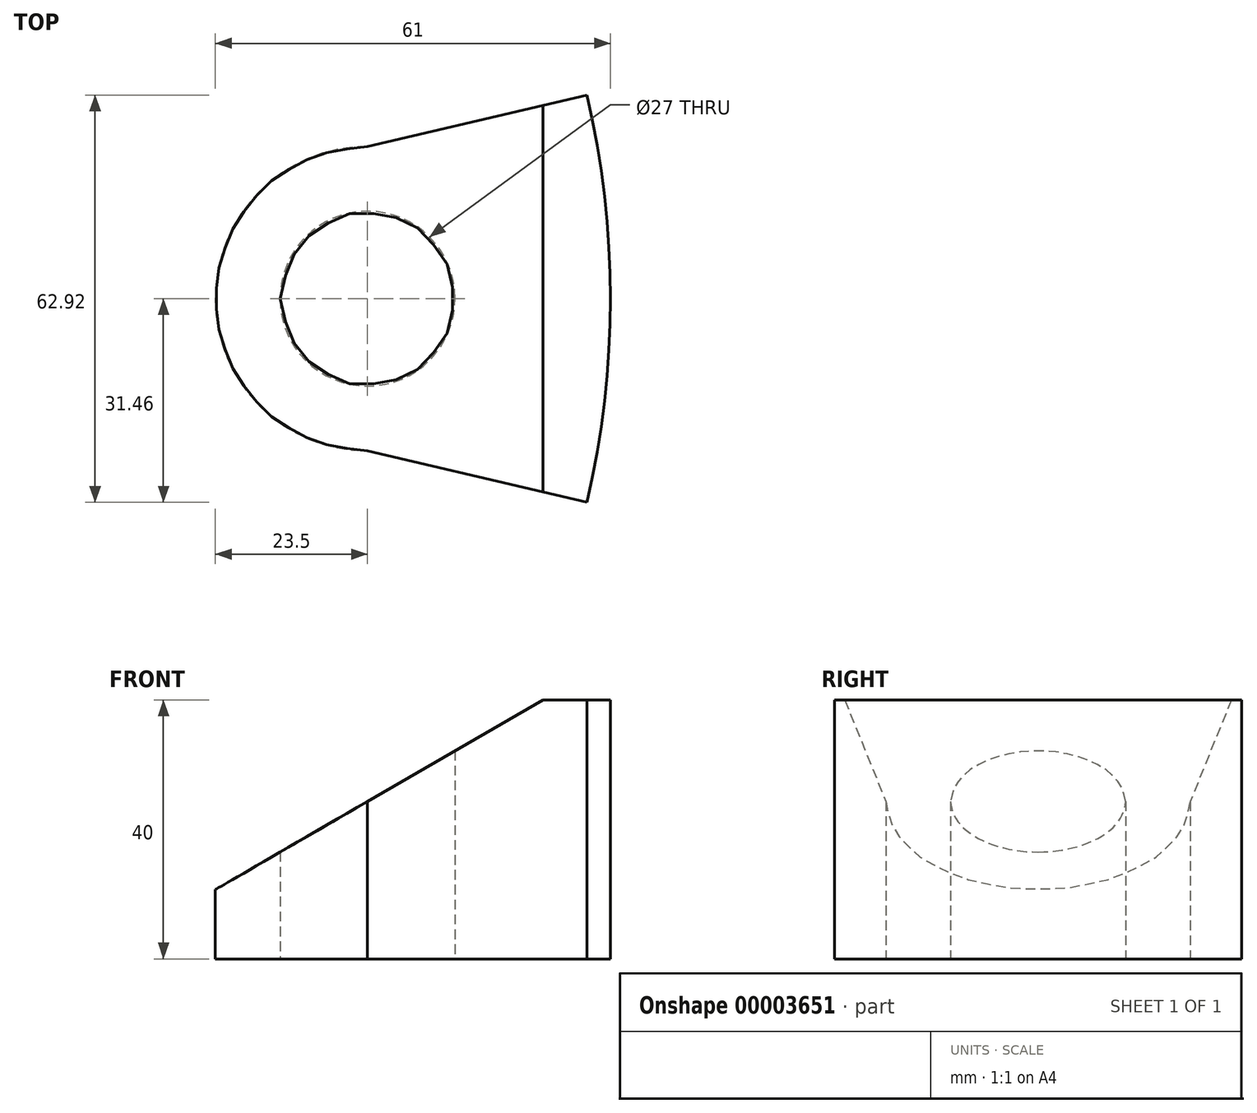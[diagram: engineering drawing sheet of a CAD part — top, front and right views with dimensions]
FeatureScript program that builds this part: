
annotation { "Feature Type Name" : "Feature", "Feature Type Description" : "" }
export const myFeature = defineFeature(function(context is Context, id is Id, definition is map)
    precondition{}
    {
        {
            var Q0;
            Q0=qCreatedBy(makeId("Top.planeOp"),FACE);
            var sketch = newSketch(context, id + "F0", { "sketchPlane" : qUnion([Q0])});
            skArc(sketch, "E0", {"start": v(133.85, -31.46) * mm, "mid": v(137.5, 0) * mm, "end": v(133.85, 31.46) * mm});
            skArc(sketch, "E1", {"start": v(128.99, -30.31) * mm, "mid": v(132.5, 0) * mm, "end": v(128.99, 30.31) * mm});
            skLineSegment(sketch, "E2", {"start": v(137.5, 0) * mm, "end": v(113.5, 0) * mm, "construction": true});
            skCircle(sketch, "E3", {"center": v(100, 0) * mm, "radius": 13.5 * mm});
            skArc(sketch, "E4.0", {"start": v(100, 23.5) * mm, "mid": v(76.5, 0) * mm, "end": v(100, -23.5) * mm});
            skLineSegment(sketch, "E5", {"start": v(100, 23.5) * mm, "end": v(128.99, 30.31) * mm});
            skLineSegment(sketch, "E6.0.MirrorCS", {"start": v(100, -23.5) * mm, "end": v(128.99, -30.31) * mm});
            skLineSegment(sketch, "E7", {"start": v(128.99, 30.31) * mm, "end": v(133.85, 31.46) * mm});
            skLineSegment(sketch, "E8.0.MirrorCS", {"start": v(128.99, -30.31) * mm, "end": v(133.85, -31.46) * mm});
            skSolve(sketch);
        }
        {
            var Q0;
            Q0 = qSketchRegion(id + "F0", true);
            extrude(context, id + "F1", {"entities" : qUnion([Q0]), "depth" : 40 * mm});
        }
        {
            var Q0;
            Q0=qCreatedBy(makeId("Front.planeOp"),FACE);
            cPlane(context, id + "F2", {"entities" : qUnion([Q0]), "cplaneType" : CPlaneType.OFFSET, "offset" : 40 * mm, "width" : 150 * mm, "height" : 150 * mm});
        }
        {
            var Q0;
            Q0=qCreatedBy(id+"F2.planeOp",FACE);
            var sketch = newSketch(context, id + "F3", { "sketchPlane" : qUnion([Q0])});
            skLineSegment(sketch, "E9", {"start": v(74.6, 9.6) * mm, "end": v(130.67, 42.1) * mm});
            skLineSegment(sketch, "E10", {"start": v(74.6, 42.1) * mm, "end": v(130.67, 42.1) * mm});
            skLineSegment(sketch, "E11", {"start": v(74.6, 9.6) * mm, "end": v(74.6, 42.1) * mm});
            skSolve(sketch);
        }
        {
            var Q0;
            Q0 = qSketchRegion(id + "F3", true);
            extrude(context, id + "F4", {"entities" : qUnion([Q0]), "operationType" : NewBodyOperationType.REMOVE, "oppositeDirection" : true, "depth" : 91.7 * mm});
        }
    });
